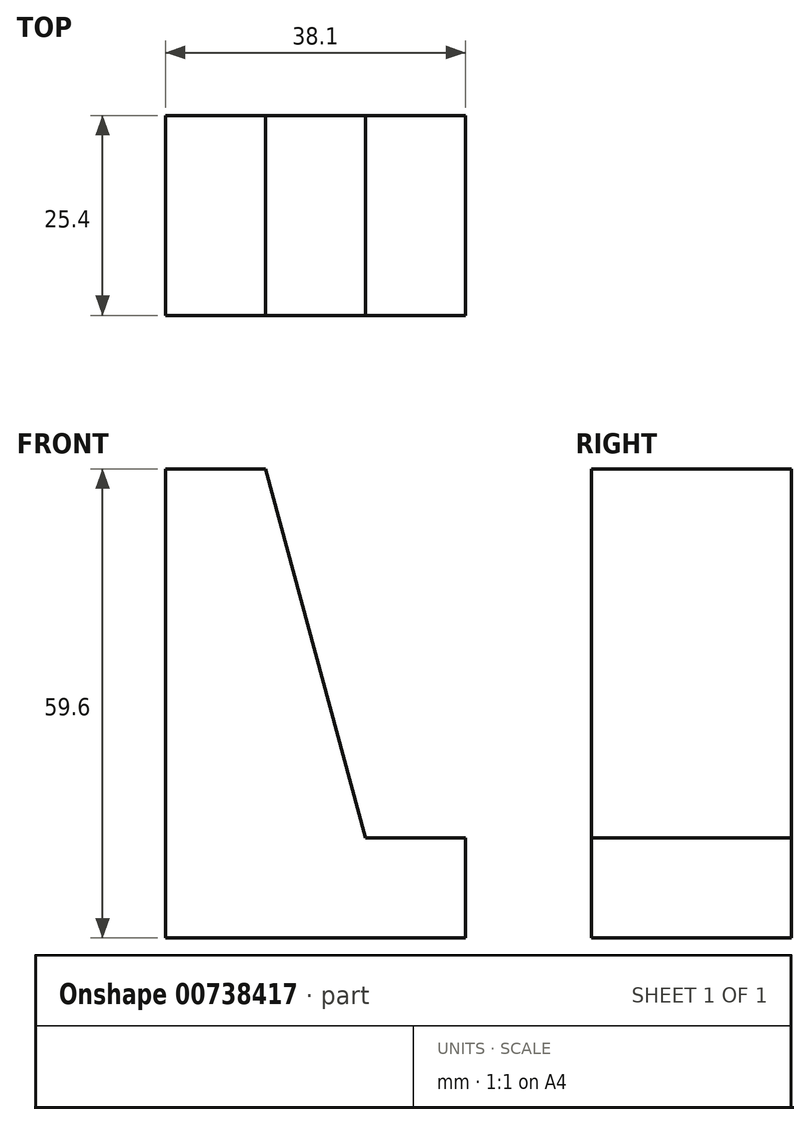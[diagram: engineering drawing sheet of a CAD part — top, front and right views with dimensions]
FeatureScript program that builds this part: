
annotation { "Feature Type Name" : "Feature", "Feature Type Description" : "" }
export const myFeature = defineFeature(function(context is Context, id is Id, definition is map)
    precondition{}
    {
        {
            var Q0;
            Q0=qCreatedBy(makeId("Front.planeOp"),FACE);
            var sketch = newSketch(context, id + "F0", { "sketchPlane" : qUnion([Q0])});
            skLineSegment(sketch, "E0", {"start": v(0, 59.6) * mm, "end": v(0, 0) * mm});
            skLineSegment(sketch, "E1", {"start": v(0, 0) * mm, "end": v(38.1, 0) * mm});
            skLineSegment(sketch, "E2", {"start": v(38.1, 0) * mm, "end": v(38.1, 12.7) * mm});
            skLineSegment(sketch, "E3", {"start": v(38.1, 12.7) * mm, "end": v(25.4, 12.7) * mm});
            skLineSegment(sketch, "E4", {"start": v(25.4, 12.7) * mm, "end": v(12.7, 59.6) * mm});
            skLineSegment(sketch, "E5", {"start": v(12.7, 59.6) * mm, "end": v(0, 59.6) * mm});
            skSolve(sketch);
        }
        {
            var Q0;
            Q0 = qSketchRegion(id + "F0", true);
            extrude(context, id + "F1", {"entities" : qUnion([Q0]), "depth" : 25.4 * mm, "offsetDistance" : 25.4 * mm});
        }
    });
